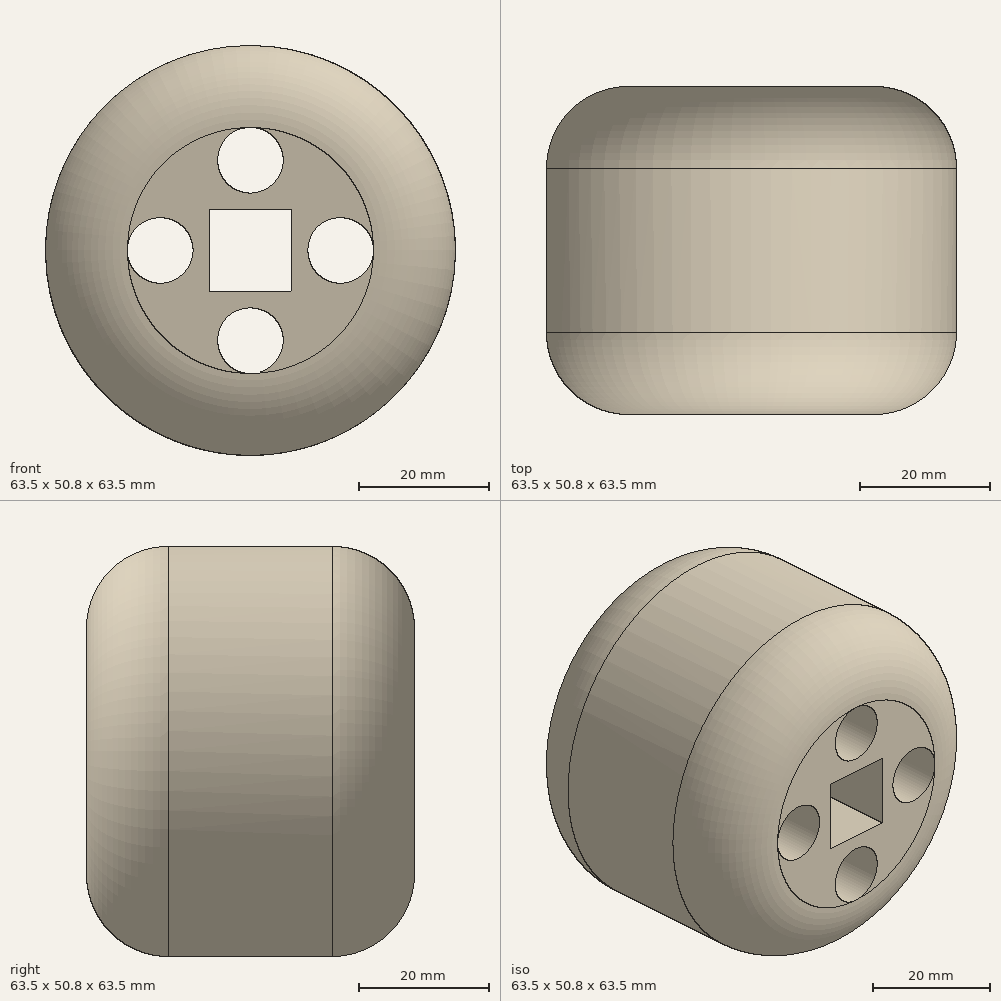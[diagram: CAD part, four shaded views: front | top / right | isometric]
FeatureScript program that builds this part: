
annotation { "Feature Type Name" : "Feature", "Feature Type Description" : "" }
export const myFeature = defineFeature(function(context is Context, id is Id, definition is map)
    precondition{}
    {
        {
            var Q0;
            Q0=qCreatedBy(makeId("Front.planeOp"),FACE);
            var sketch = newSketch(context, id + "F0", { "sketchPlane" : qUnion([Q0])});
            skCircle(sketch, "E0", {"center": v(0, 0) * mm, "radius": 31.75 * mm});
            skSolve(sketch);
        }
        {
            var Q0;
            Q0=makeQuery(id+"F0.imprint","IMPRINT",FACE,{"disambiguationData":[TD([[makeQuery(id+"F0.imprint","IMPRINT",EDGE,{"derivedFrom":sQuery(id+"F0.wireOp",EDGE,"E0")}),1.0]])]});
            extrude(context, id + "F1", {"entities" : qUnion([Q0]), "depth" : 25.4 * mm});
        }
        {
            var Q0;
            Q0=qCreatedBy(makeId("Front.planeOp"),FACE);
            var sketch = newSketch(context, id + "F2", { "sketchPlane" : qUnion([Q0])});
            skCircle(sketch, "E1", {"center": v(0, 13.97) * mm, "radius": 5.08 * mm});
            skCircle(sketch, "E2", {"center": v(13.97, 0) * mm, "radius": 5.08 * mm});
            skCircle(sketch, "E3", {"center": v(0, -13.97) * mm, "radius": 5.08 * mm});
            skCircle(sketch, "E4", {"center": v(-13.97, 0) * mm, "radius": 5.08 * mm});
            skSolve(sketch);
        }
        {
            var Q0;
            Q0=qSketchRegion(id+"F2",true);
            extrude(context, id + "F3", {"entities" : qUnion([Q0]), "operationType" : NewBodyOperationType.REMOVE, "endBound" : BoundingType.THROUGH_ALL, "depth" : 25.4 * mm});
        }
        {
            var Q0;
            Q0=makeQuery(id+"F1.opExtrude","SWEPT_BODY",BODY,{"disambiguationData":[OSD([sQuery(id+"F0.wireOp",EDGE,"E0")])]});
            var Q1;
            Q1=qCreatedBy(makeId("Front.planeOp"),FACE);
            mirror(context, id + "F4", {"operationType" : NewBodyOperationType.ADD, "entities" : qUnion([Q0]), "mirrorPlane" : qUnion([Q1])});
        }
        {
            var Q0;
            {var subQ0=makeQuery(id+"F1.opExtrude","SWEPT_FACE",FACE,{"disambiguationData":[OSD([sQuery(id+"F0.wireOp",EDGE,"E0")])]});Q0=makeQuery(id+"F4.boolean.opBoolean","MERGE",FACE,{"derivedFrom":[subQ0,makeQuery(id+"F4.opPattern","COPY",FACE,{"derivedFrom":subQ0,"instanceName":"1"})]});}
            fillet(context, id + "F5", {"entities" : qUnion([Q0]), "radius" : 12.7 * mm, "tangentPropagation" : true, "allowEdgeOverflow" : false});
        }
        {
            var Q0;
            Q0=makeQuery(id+"F4.opPattern","COPY",FACE,{"derivedFrom":makeQuery(id+"F1WZldC2OBy5vvg_1.boolean.opBoolean","MERGE",FACE,{"derivedFrom":[makeQuery(id+"FmBiZJzzj11etu3_1.boolean.opBoolean","MERGE",FACE,{"derivedFrom":[makeQuery(id+"F1.opExtrude","CAP_FACE",FACE,{"disambiguationData":[OSD([sQuery(id+"F0.wireOp",EDGE,"E0")])],"isStart":false}),makeQuery(id+"FmBiZJzzj11etu3_1.opExtrude","CAP_FACE",FACE,{"disambiguationData":[OSD([sQuery(id+"Ft8lbblbWyurPbU_1.wireOp",EDGE,"0gTzFuAu-Dfou-Arnk-xvKb-c3TsP2g5u4qN.bottom"),sQuery(id+"Ft8lbblbWyurPbU_1.wireOp",EDGE,"0gTzFuAu-Dfou-Arnk-xvKb-c3TsP2g5u4qN.top"),sQuery(id+"Ft8lbblbWyurPbU_1.wireOp",EDGE,"0gTzFuAu-Dfou-Arnk-xvKb-c3TsP2g5u4qN.left"),sQuery(id+"Ft8lbblbWyurPbU_1.wireOp",EDGE,"0gTzFuAu-Dfou-Arnk-xvKb-c3TsP2g5u4qN.right"),sQuery(id+"Ft8lbblbWyurPbU_1.wireOp",EDGE,"NJGusiZp-8W9i-ERT9-Wk8S-lUzyQzLld9we.bottom"),sQuery(id+"Ft8lbblbWyurPbU_1.wireOp",EDGE,"NJGusiZp-8W9i-ERT9-Wk8S-lUzyQzLld9we.top"),sQuery(id+"Ft8lbblbWyurPbU_1.wireOp",EDGE,"NJGusiZp-8W9i-ERT9-Wk8S-lUzyQzLld9we.left"),sQuery(id+"Ft8lbblbWyurPbU_1.wireOp",EDGE,"NJGusiZp-8W9i-ERT9-Wk8S-lUzyQzLld9we.right")])],"isStart":false})]}),makeQuery(id+"F1WZldC2OBy5vvg_1.opExtrude","CAP_FACE",FACE,{"disambiguationData":[OSD([sQuery(id+"FcW5HZdUkP2czRg_1.wireOp",EDGE,"m0DhUsYQ-ojb6-G5fo-UUYZ-vxe7LCTsh8OX")])],"isStart":false})]}),"instanceName":"1"});
            var sketch = newSketch(context, id + "F6", { "sketchPlane" : qUnion([Q0])});
            skLineSegment(sketch, "E5.bottom", {"start": v(6.35, -6.35) * mm, "end": v(-6.35, -6.35) * mm});
            skLineSegment(sketch, "E5.top", {"start": v(6.35, 6.35) * mm, "end": v(-6.35, 6.35) * mm});
            skLineSegment(sketch, "E5.left", {"start": v(6.35, -6.35) * mm, "end": v(6.35, 6.35) * mm});
            skLineSegment(sketch, "E5.right", {"start": v(-6.35, -6.35) * mm, "end": v(-6.35, 6.35) * mm});
            skPoint(sketch, "E5.middle", {"position": v(0, 0) * mm});
            skSolve(sketch);
        }
        {
            var Q0;
            Q0=makeQuery(id+"F6.imprint","IMPRINT",FACE,{"disambiguationData":[TD([[makeQuery(id+"F6.imprint","IMPRINT",EDGE,{"derivedFrom":sQuery(id+"F6.wireOp",EDGE,"E5.bottom")}),-1.0]])]});
            extrude(context, id + "F7", {"entities" : qUnion([Q0]), "operationType" : NewBodyOperationType.REMOVE, "endBound" : BoundingType.THROUGH_ALL, "oppositeDirection" : true, "depth" : 25.4 * mm});
        }
    });
